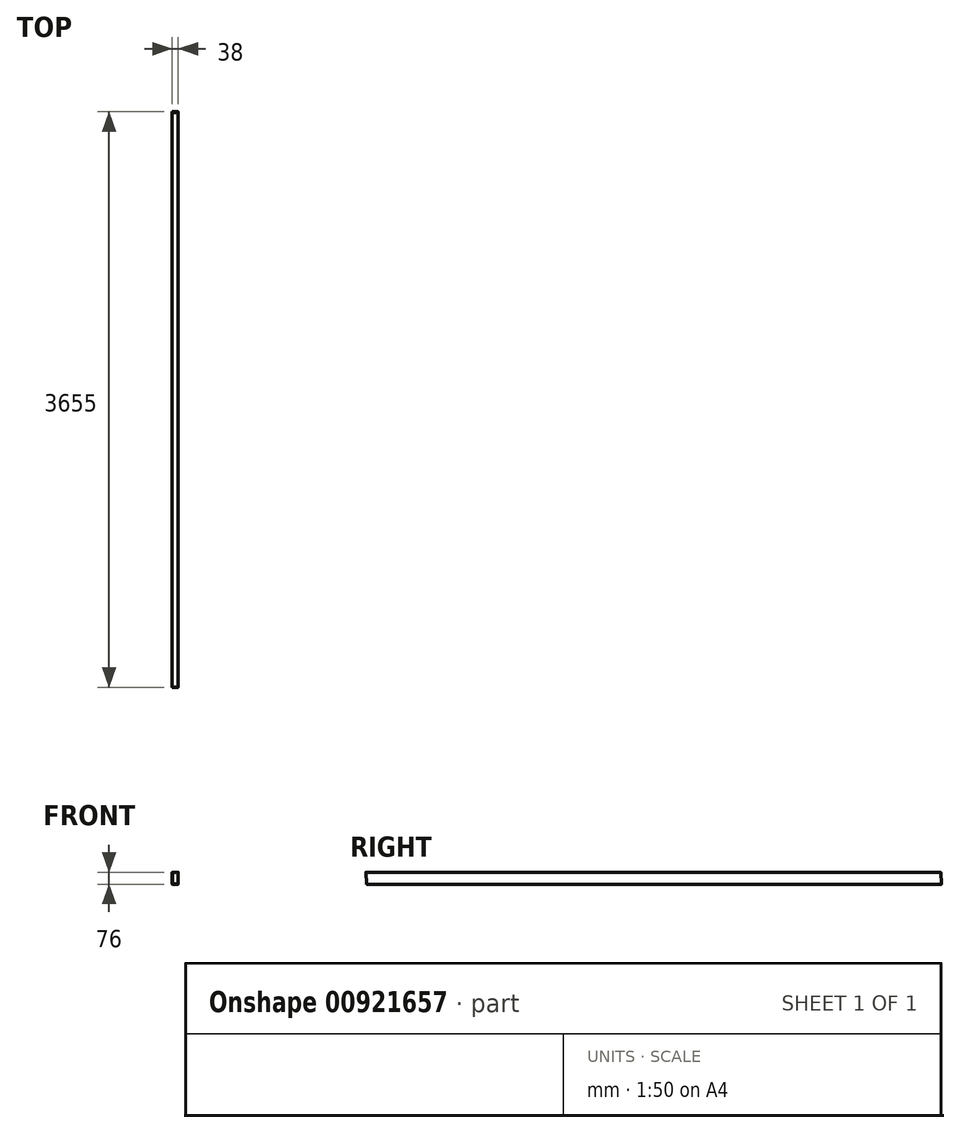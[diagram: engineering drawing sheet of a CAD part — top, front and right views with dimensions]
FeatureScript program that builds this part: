
annotation { "Feature Type Name" : "Feature", "Feature Type Description" : "" }
export const myFeature = defineFeature(function(context is Context, id is Id, definition is map)
    precondition{}
    {
        {
            var Q0;
            Q0=qCreatedBy(makeId("Front.planeOp"),FACE);
            var sketch = newSketch(context, id + "F0", { "sketchPlane" : qUnion([Q0])});
            skLineSegment(sketch, "E0.bottom", {"start": v(2, 0) * mm, "end": v(36, 0) * mm});
            skLineSegment(sketch, "E0.top", {"start": v(2, 76) * mm, "end": v(36, 76) * mm});
            skLineSegment(sketch, "E0.left", {"start": v(0, 2) * mm, "end": v(0, 74) * mm});
            skLineSegment(sketch, "E0.right", {"start": v(38, 2) * mm, "end": v(38, 74) * mm});
            skLineSegment(sketch, "E1.0", {"start": v(2, 4) * mm, "end": v(2, 72) * mm});
            skLineSegment(sketch, "E2.0", {"start": v(4, 74) * mm, "end": v(34, 74) * mm});
            skLineSegment(sketch, "E3.0", {"start": v(36, 4) * mm, "end": v(36, 72) * mm});
            skLineSegment(sketch, "E4.0", {"start": v(4, 2) * mm, "end": v(34, 2) * mm});
            skPoint(sketch, "E5.visualSharp", {"position": v(0, 0) * mm});
            skArc(sketch, "E5.filletArc", {"start": v(0, 2) * mm, "mid": v(0.59, 0.59) * mm, "end": v(2, 0) * mm});
            skArc(sketch, "E6.filletArc", {"start": v(2, 4) * mm, "mid": v(2.59, 2.59) * mm, "end": v(4, 2) * mm});
            skPoint(sketch, "E7.visualSharp", {"position": v(36, 2) * mm});
            skArc(sketch, "E7.filletArc", {"start": v(34, 2) * mm, "mid": v(35.41, 2.59) * mm, "end": v(36, 4) * mm});
            skPoint(sketch, "E8.visualSharp", {"position": v(38, 0) * mm});
            skArc(sketch, "E8.filletArc", {"start": v(36, 0) * mm, "mid": v(37.41, 0.59) * mm, "end": v(38, 2) * mm});
            skPoint(sketch, "E9.visualSharp", {"position": v(38, 76) * mm});
            skArc(sketch, "E9.filletArc", {"start": v(38, 74) * mm, "mid": v(37.41, 75.41) * mm, "end": v(36, 76) * mm});
            skArc(sketch, "E10.filletArc", {"start": v(36, 72) * mm, "mid": v(35.41, 73.41) * mm, "end": v(34, 74) * mm});
            skPoint(sketch, "E11.visualSharp", {"position": v(0, 76) * mm});
            skArc(sketch, "E11.filletArc", {"start": v(2, 76) * mm, "mid": v(0.59, 75.41) * mm, "end": v(0, 74) * mm});
            skArc(sketch, "E12.filletArc", {"start": v(4, 74) * mm, "mid": v(2.59, 73.41) * mm, "end": v(2, 72) * mm});
            skSolve(sketch);
        }
        {
            var Q0;
            Q0 = qSketchRegion(id + "F0", true);
            extrude(context, id + "F1", {"entities" : qUnion([Q0]), "depth" : 3655 * mm, "offsetDistance" : 25 * mm});
        }
        {
            var Q0;
            Q0=makeQuery(id+"F1.opExtrude","SWEPT_FACE",FACE,{"disambiguationData":[OSD([sQuery(id+"F0.wireOp",EDGE,"E0.right")])]});
            var sketch = newSketch(context, id + "F2", { "sketchPlane" : qUnion([Q0])});
            skLineSegment(sketch, "E13", {"start": v(0, 0) * mm, "end": v(-3.81, 76.27) * mm});
            skLineSegment(sketch, "E14", {"start": v(-3.81, 76.27) * mm, "end": v(0, 76.46) * mm});
            skPoint(sketch, "E15.start.orphan", {"position": v(0, 38) * mm});
            skLineSegment(sketch, "E16", {"start": v(0, 76.46) * mm, "end": v(0, 0) * mm});
            skSolve(sketch);
        }
        {
            var Q0;
            Q0 = qSketchRegion(id + "F2", true);
            extrude(context, id + "F3", {"entities" : qUnion([Q0]), "operationType" : NewBodyOperationType.REMOVE, "oppositeDirection" : true, "depth" : 38 * mm, "offsetDistance" : 25 * mm});
        }
        {
            var Q0;
            Q0=makeQuery(id+"F1.opExtrude","SWEPT_FACE",FACE,{"disambiguationData":[OSD([sQuery(id+"F0.wireOp",EDGE,"E0.right")])]});
            var sketch = newSketch(context, id + "F4", { "sketchPlane" : qUnion([Q0])});
            skLineSegment(sketch, "E17", {"start": v(-3655, 0) * mm, "end": v(-3651.2, 0) * mm});
            skLineSegment(sketch, "E18", {"start": v(-3651.2, 0) * mm, "end": v(-3655, 76.02) * mm});
            skPoint(sketch, "E19.end.orphan", {"position": v(-3655, 38) * mm});
            skLineSegment(sketch, "E20", {"start": v(-3655, 76.02) * mm, "end": v(-3655, 0) * mm});
            skSolve(sketch);
        }
        {
            var Q0;
            Q0 = qSketchRegion(id + "F4", true);
            extrude(context, id + "F5", {"entities" : qUnion([Q0]), "operationType" : NewBodyOperationType.REMOVE, "oppositeDirection" : true, "depth" : 38 * mm, "offsetDistance" : 25 * mm});
        }
    });
